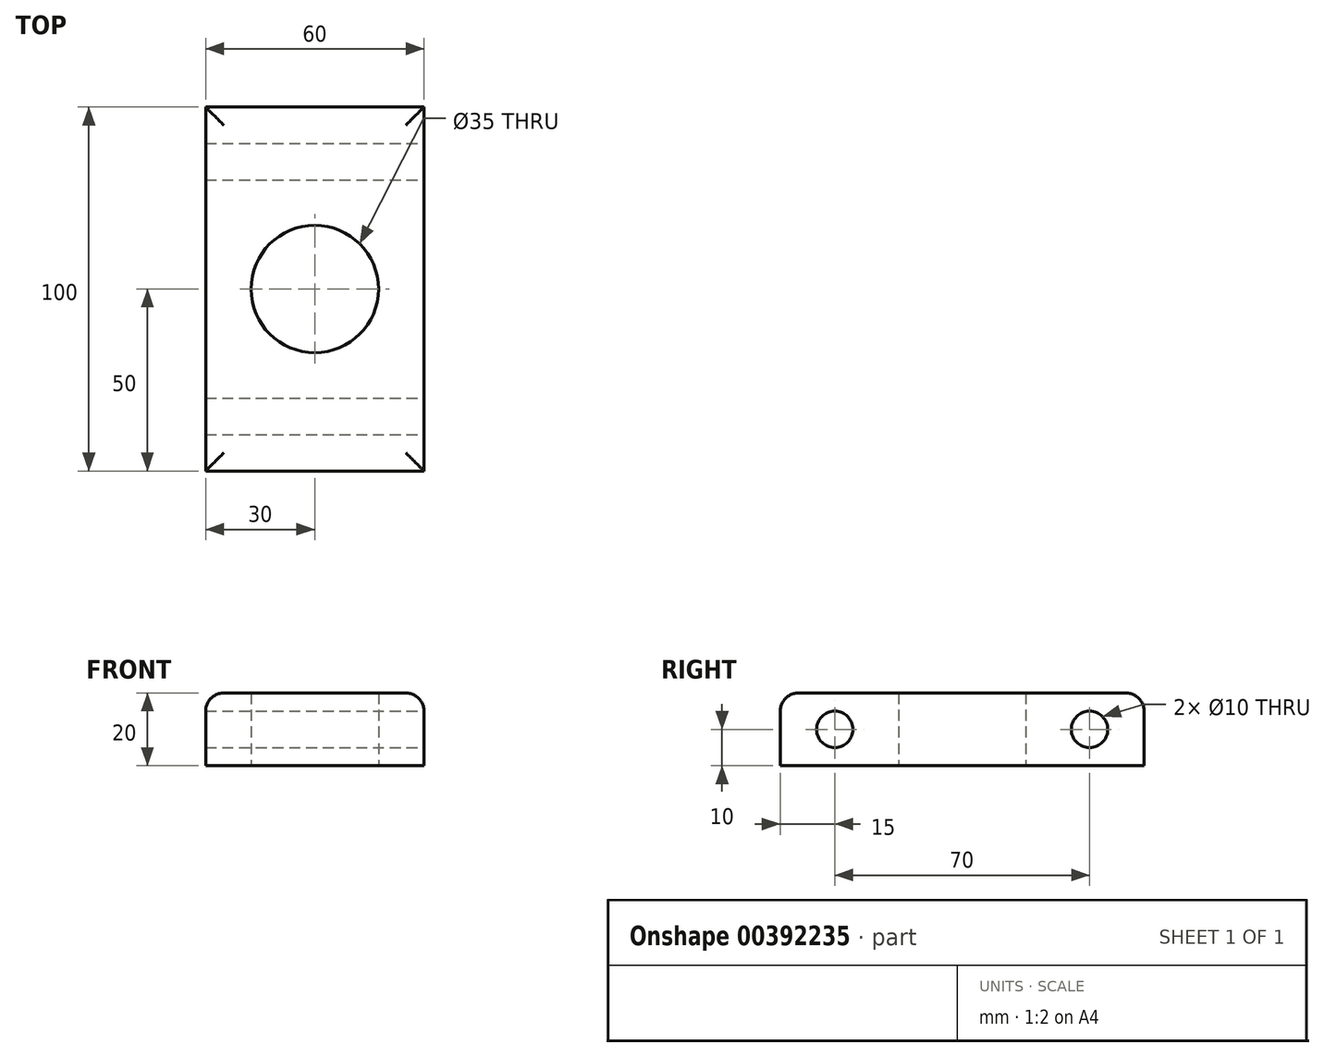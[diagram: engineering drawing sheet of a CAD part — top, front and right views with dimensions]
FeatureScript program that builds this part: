
annotation { "Feature Type Name" : "Feature", "Feature Type Description" : "" }
export const myFeature = defineFeature(function(context is Context, id is Id, definition is map)
    precondition{}
    {
        {
            var Q0;
            Q0=qCreatedBy(makeId("Top.planeOp"),FACE);
            var sketch = newSketch(context, id + "F0", { "sketchPlane" : qUnion([Q0])});
            skLineSegment(sketch, "E0.bottom", {"start": v(-30, -50) * mm, "end": v(30, -50) * mm});
            skLineSegment(sketch, "E0.top", {"start": v(-30, 50) * mm, "end": v(30, 50) * mm});
            skLineSegment(sketch, "E0.left", {"start": v(-30, -50) * mm, "end": v(-30, 50) * mm});
            skLineSegment(sketch, "E0.right", {"start": v(30, -50) * mm, "end": v(30, 50) * mm});
            skCircle(sketch, "E1", {"center": v(0, 0) * mm, "radius": 17.5 * mm});
            skSolve(sketch);
        }
        {
            var Q0;
            Q0=makeQuery(id+"F0.imprint","IMPRINT",FACE,{"disambiguationData":[TD([[makeQuery(id+"F0.imprint","IMPRINT",EDGE,{"derivedFrom":sQuery(id+"F0.wireOp",EDGE,"E0.bottom")}),1.0]])]});
            extrude(context, id + "F1", {"entities" : qUnion([Q0]), "depth" : 20 * mm});
        }
        {
            var Q0;
            Q0=makeQuery(id+"F1.opExtrude","SWEPT_FACE",FACE,{"disambiguationData":[OSD([sQuery(id+"F0.wireOp",EDGE,"E0.right")])]});
            var sketch = newSketch(context, id + "F2", { "sketchPlane" : qUnion([Q0])});
            skCircle(sketch, "E2", {"center": v(-35, 10) * mm, "radius": 5 * mm});
            skCircle(sketch, "E3", {"center": v(35, 10) * mm, "radius": 5 * mm});
            skLineSegment(sketch, "E4", {"start": v(-50, 10) * mm, "end": v(50, 10) * mm, "construction": true});
            skSolve(sketch);
        }
        {
            var Q0;
            Q0=makeQuery(id+"F2.imprint","IMPRINT",FACE,{"disambiguationData":[TD([[makeQuery(id+"F2.imprint","IMPRINT",EDGE,{"derivedFrom":sQuery(id+"F2.wireOp",EDGE,"E2")}),-1.0]])]});
            var Q1;
            Q1=sQuery(id+"F2.wireOp",EDGE,"E3");
            extrude(context, id + "F3", {"entities" : qUnion([Q0]), "operationType" : NewBodyOperationType.INTERSECT, "surfaceEntities" : qUnion([Q1]), "oppositeDirection" : true, "depth" : 100 * mm});
        }
        {
            var Q0;
            Q0=makeQuery(id+"F1.opExtrude","CAP_EDGE",EDGE,{"disambiguationData":[OSD([sQuery(id+"F0.wireOp",EDGE,"E0.right")])],"isStart":false});
            var Q1;
            Q1=makeQuery(id+"F1.opExtrude","CAP_EDGE",EDGE,{"disambiguationData":[OSD([sQuery(id+"F0.wireOp",EDGE,"E0.bottom")])],"isStart":false});
            var Q2;
            Q2=makeQuery(id+"F1.opExtrude","CAP_EDGE",EDGE,{"disambiguationData":[OSD([sQuery(id+"F0.wireOp",EDGE,"E0.left")])],"isStart":false});
            var Q3;
            Q3=makeQuery(id+"F1.opExtrude","CAP_EDGE",EDGE,{"disambiguationData":[OSD([sQuery(id+"F0.wireOp",EDGE,"E0.top")])],"isStart":false});
            fillet(context, id + "F4", {"entities" : qUnion([Q0, Q1, Q2, Q3]), "radius" : 5 * mm, "tangentPropagation" : true, "allowEdgeOverflow" : false});
        }
    });
